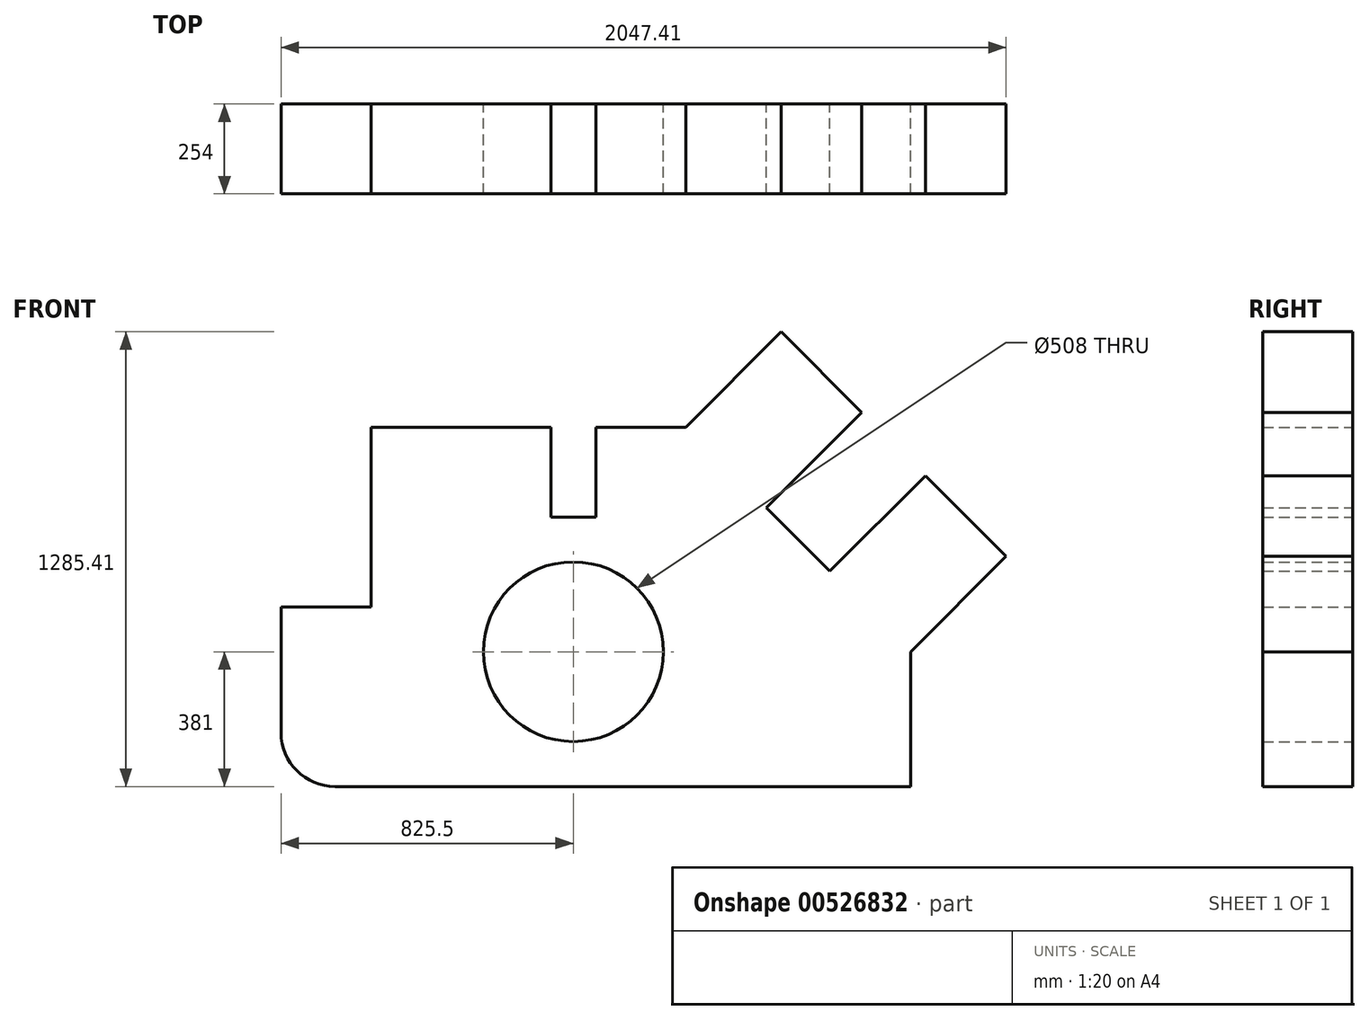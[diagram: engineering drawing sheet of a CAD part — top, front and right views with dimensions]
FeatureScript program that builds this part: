
annotation { "Feature Type Name" : "Feature", "Feature Type Description" : "" }
export const myFeature = defineFeature(function(context is Context, id is Id, definition is map)
    precondition{}
    {
        {
            var Q0;
            Q0=qCreatedBy(makeId("Front.planeOp"),FACE);
            var sketch = newSketch(context, id + "F0", { "sketchPlane" : qUnion([Q0])});
            skLineSegment(sketch, "E0", {"start": v(152.4, 0) * mm, "end": v(1778, 0) * mm});
            skLineSegment(sketch, "E1", {"start": v(1778, 0) * mm, "end": v(1778, 381) * mm});
            skLineSegment(sketch, "E2", {"start": v(0, 152.4) * mm, "end": v(0, 508) * mm});
            skPoint(sketch, "E3.visualSharp", {"position": v(0, 0) * mm});
            skArc(sketch, "E3.filletArc", {"start": v(0, 152.4) * mm, "mid": v(44.64, 44.64) * mm, "end": v(152.4, 0) * mm});
            skCircle(sketch, "E4", {"center": v(825.5, 381) * mm, "radius": 254 * mm});
            skLineSegment(sketch, "E5", {"start": v(0, 508) * mm, "end": v(254, 508) * mm});
            skLineSegment(sketch, "E6", {"start": v(254, 508) * mm, "end": v(254, 1016) * mm});
            skLineSegment(sketch, "E7", {"start": v(254, 1016) * mm, "end": v(762, 1016) * mm});
            skLineSegment(sketch, "E8", {"start": v(762, 1016) * mm, "end": v(762, 762) * mm});
            skLineSegment(sketch, "E9", {"start": v(762, 762) * mm, "end": v(889, 762) * mm});
            skLineSegment(sketch, "E10", {"start": v(889, 762) * mm, "end": v(889, 1016) * mm});
            skLineSegment(sketch, "E11", {"start": v(889, 1016) * mm, "end": v(1143, 1016) * mm});
            skLineSegment(sketch, "E12", {"start": v(1778, 381) * mm, "end": v(2047.4, 650.4) * mm});
            skLineSegment(sketch, "E13", {"start": v(2047.4, 650.4) * mm, "end": v(1819.71, 878.1) * mm});
            skLineSegment(sketch, "E14", {"start": v(1819.71, 878.1) * mm, "end": v(1550.3, 608.7) * mm});
            skLineSegment(sketch, "E15", {"start": v(1550.3, 608.7) * mm, "end": v(1370.7, 788.3) * mm});
            skLineSegment(sketch, "E16", {"start": v(1370.7, 788.3) * mm, "end": v(1640.1, 1057.71) * mm});
            skLineSegment(sketch, "E17", {"start": v(1640.1, 1057.71) * mm, "end": v(1412.4, 1285.4) * mm});
            skLineSegment(sketch, "E18", {"start": v(1143, 1016) * mm, "end": v(1412.4, 1285.4) * mm});
            skSolve(sketch);
        }
        {
            var Q0;
            Q0=makeQuery(id+"F0.imprint","IMPRINT",FACE,{"disambiguationData":[TD([[makeQuery(id+"F0.imprint","IMPRINT",EDGE,{"derivedFrom":sQuery(id+"F0.wireOp",EDGE,"E0")}),1.0]])]});
            extrude(context, id + "F1", {"entities" : qUnion([Q0]), "depth" : 254 * mm, "offsetDistance" : 25.4 * mm});
        }
    });
